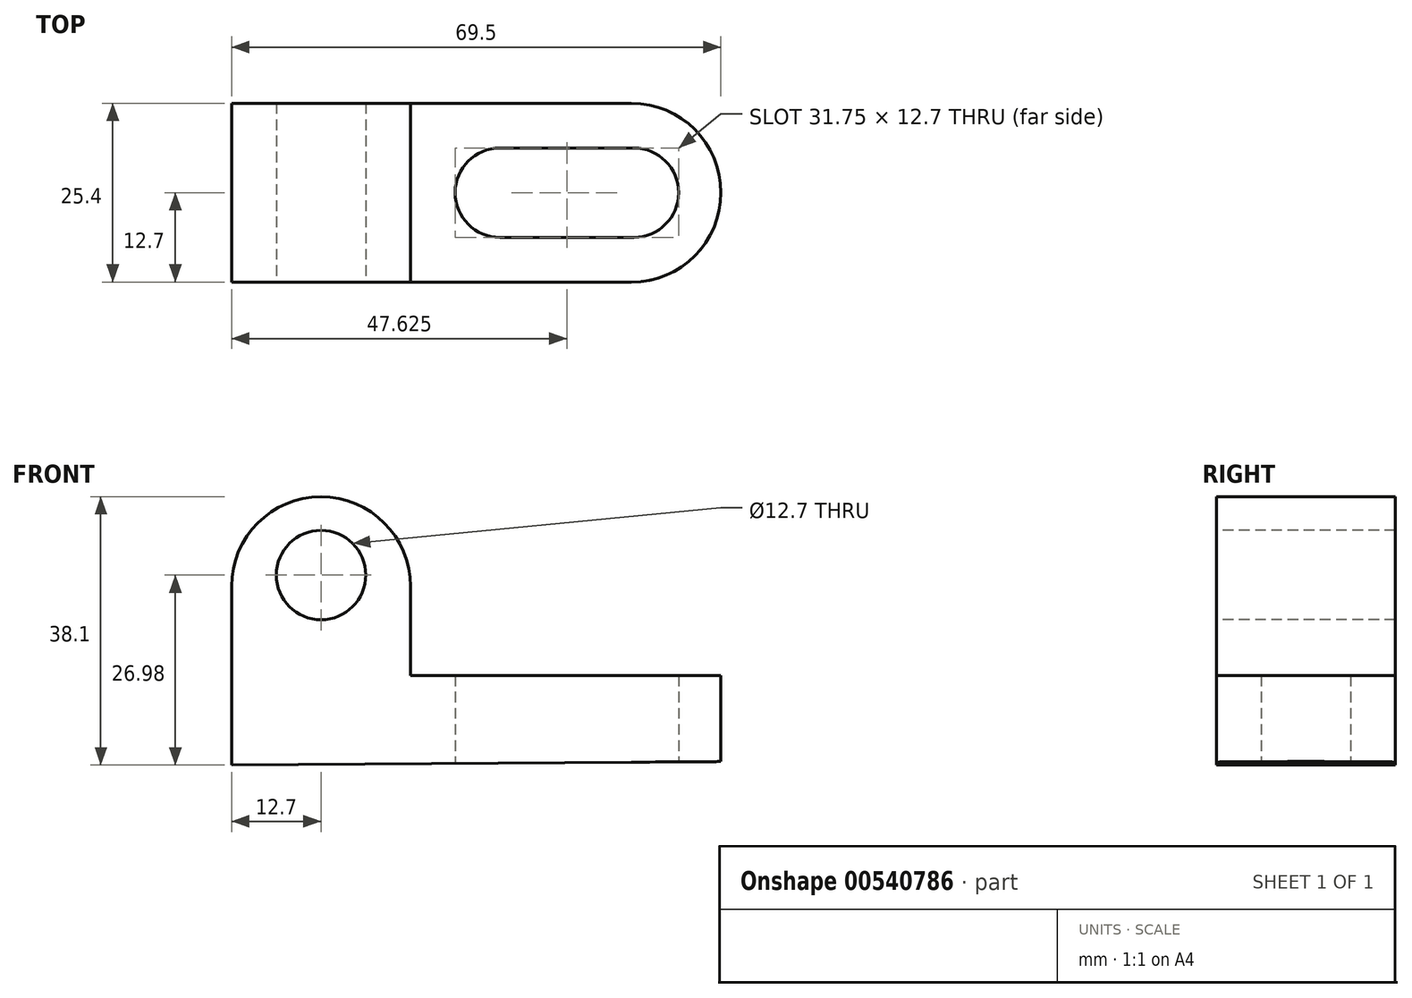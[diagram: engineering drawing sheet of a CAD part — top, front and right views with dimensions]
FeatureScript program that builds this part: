
annotation { "Feature Type Name" : "Feature", "Feature Type Description" : "" }
export const myFeature = defineFeature(function(context is Context, id is Id, definition is map)
    precondition{}
    {
        {
            var Q0;
            Q0=qCreatedBy(makeId("Front.planeOp"),FACE);
            var sketch = newSketch(context, id + "F0", { "sketchPlane" : qUnion([Q0])});
            skLineSegment(sketch, "E0", {"start": v(0, 38.1) * mm, "end": v(0, 0) * mm});
            skLineSegment(sketch, "E1", {"start": v(0, 38.1) * mm, "end": v(25.4, 38.1) * mm});
            skLineSegment(sketch, "E2", {"start": v(25.4, 38.1) * mm, "end": v(25.4, 12.7) * mm});
            skLineSegment(sketch, "E3", {"start": v(25.05, 12.7) * mm, "end": v(69.5, 12.7) * mm});
            skLineSegment(sketch, "E4", {"start": v(69.5, 12.7) * mm, "end": v(69.5, 0) * mm});
            skLineSegment(sketch, "E5", {"start": v(69.85, 0.49) * mm, "end": v(0, 0) * mm});
            skSolve(sketch);
        }
        {
            var Q0;
            {var subQ4=sQuery(id+"F0.wireOp",EDGE,"E0");Q0=makeQuery(id+"F0.imprint","IMPRINT",FACE,{"disambiguationData":[TD([[makeQuery(id+"F0.imprint","IMPRINT",EDGE,{"derivedFrom":subQ4}),1.0]])]});}
            extrude(context, id + "F1", {"entities" : qUnion([Q0]), "depth" : 25.4 * mm, "offsetDistance" : 25.4 * mm});
        }
        {
            var Q0;
            Q0=makeQuery(id+"F1.opExtrude","SWEPT_FACE",FACE,{"disambiguationData":[OSD([sQuery(id+"F0.wireOp",EDGE,"E3")])]});
            var sketch = newSketch(context, id + "F2", { "sketchPlane" : qUnion([Q0])});
            skLineSegment(sketch, "E6", {"start": v(69.5, -25.4) * mm, "end": v(56.8, -25.4) * mm});
            skLineSegment(sketch, "E7", {"start": v(69.5, 0) * mm, "end": v(56.8, 0) * mm});
            skArc(sketch, "E8", {"start": v(56.8, -25.4) * mm, "mid": v(69.5, -12.7) * mm, "end": v(56.8, 0) * mm});
            skSolve(sketch);
        }
        {
            var Q0;
            {var subQ0=sQuery(id+"F2.wireOp",EDGE,"E7");Q0=makeQuery(id+"F2.imprint","IMPRINT",FACE,{"disambiguationData":[TD([[makeQuery(id+"F2.imprint","IMPRINT",EDGE,{"derivedFrom":subQ0}),-1.0]])]});}
            var Q1;
            {var subQ0=sQuery(id+"F2.wireOp",EDGE,"E6");Q1=makeQuery(id+"F2.imprint","IMPRINT",FACE,{"disambiguationData":[TD([[makeQuery(id+"F2.imprint","IMPRINT",EDGE,{"derivedFrom":subQ0}),1.0]])]});}
            extrude(context, id + "F3", {"entities" : qUnion([Q0, Q1]), "operationType" : NewBodyOperationType.REMOVE, "oppositeDirection" : true, "depth" : 25.4 * mm, "offsetDistance" : 25.4 * mm});
        }
        {
            var Q0;
            Q0=makeQuery(id+"F1.opExtrude","CAP_FACE",FACE,{"disambiguationData":[OSD([sQuery(id+"F0.wireOp",EDGE,"E0"),sQuery(id+"F0.wireOp",EDGE,"E1"),sQuery(id+"F0.wireOp",EDGE,"E2"),sQuery(id+"F0.wireOp",EDGE,"E3"),sQuery(id+"F0.wireOp",EDGE,"E4"),sQuery(id+"F0.wireOp",EDGE,"E5")])],"isStart":false});
            var sketch = newSketch(context, id + "F4", { "sketchPlane" : qUnion([Q0])});
            skCircle(sketch, "E9", {"center": v(12.7, 26.98) * mm, "radius": 6.35 * mm});
            skLineSegment(sketch, "E10", {"start": v(12.7, 26.98) * mm, "end": v(19.05, 26.98) * mm});
            skLineSegment(sketch, "E11", {"start": v(6.36, 27.28) * mm, "end": v(0, 27.28) * mm});
            skLineSegment(sketch, "E12", {"start": v(19.05, 26.98) * mm, "end": v(25.4, 26.98) * mm});
            skSolve(sketch);
        }
        {
            var Q0;
            {var subQ0=sQuery(id+"F4.wireOp",EDGE,"E9");var subQ1=makeQuery(id+"F4.imprint","INTERSECT",VERTEX,{"derivedFrom":[subQ0,sQuery(id+"F4.wireOp",EDGE,"E12")]});Q0=makeQuery(id+"F4.imprint","IMPRINT",FACE,{"disambiguationData":[TD([[makeQuery(id+"F4.imprint","IMPRINT",EDGE,{"disambiguationData":[TD([[subQ1,-1.0]])],"derivedFrom":subQ0}),1.0]])]});}
            extrude(context, id + "F5", {"entities" : qUnion([Q0]), "operationType" : NewBodyOperationType.REMOVE, "oppositeDirection" : true, "depth" : 101.6 * mm, "offsetDistance" : 25.4 * mm});
        }
        {
            var Q0;
            Q0=makeQuery(id+"F1.opExtrude","CAP_FACE",FACE,{"disambiguationData":[OSD([sQuery(id+"F0.wireOp",EDGE,"E0"),sQuery(id+"F0.wireOp",EDGE,"E1"),sQuery(id+"F0.wireOp",EDGE,"E2"),sQuery(id+"F0.wireOp",EDGE,"E3"),sQuery(id+"F0.wireOp",EDGE,"E4"),sQuery(id+"F0.wireOp",EDGE,"E5")])],"isStart":false});
            var sketch = newSketch(context, id + "F6", { "sketchPlane" : qUnion([Q0])});
            skArc(sketch, "E13", {"start": v(25.4, 25.4) * mm, "mid": v(12.7, 38.1) * mm, "end": v(0, 25.4) * mm});
            skLineSegment(sketch, "E14", {"start": v(12.7, 25.4) * mm, "end": v(12.7, 38.1) * mm});
            skLineSegment(sketch, "E15", {"start": v(0, 25.4) * mm, "end": v(0, 0) * mm});
            skLineSegment(sketch, "E16", {"start": v(25.4, 25.4) * mm, "end": v(25.4, 0) * mm});
            skSolve(sketch);
        }
        {
            var Q0;
            {var subQ1=makeQuery(id+"F1.opExtrude","CAP_EDGE",EDGE,{"disambiguationData":[OSD([sQuery(id+"F0.wireOp",EDGE,"E2")])],"isStart":false});var subQ3=makeQuery(id+"F1.opExtrude","CAP_EDGE",EDGE,{"disambiguationData":[OSD([sQuery(id+"F0.wireOp",EDGE,"E1")])],"isStart":false});var subQ5=makeQuery(id+"F6.imprint","INTERSECT",VERTEX,{"derivedFrom":[subQ3,subQ1]});Q0=makeQuery(id+"F6.imprint","IMPRINT",FACE,{"disambiguationData":[TD([[makeQuery(id+"F6.imprint","IMPRINT",EDGE,{"disambiguationData":[TD([[subQ5,1.0]])],"derivedFrom":subQ3}),-1.0]])]});}
            var Q1;
            {var subQ1=makeQuery(id+"F1.opExtrude","CAP_EDGE",EDGE,{"disambiguationData":[OSD([sQuery(id+"F0.wireOp",EDGE,"E0")])],"isStart":false});var subQ3=makeQuery(id+"F1.opExtrude","CAP_EDGE",EDGE,{"disambiguationData":[OSD([sQuery(id+"F0.wireOp",EDGE,"E1")])],"isStart":false});var subQ5=makeQuery(id+"F6.imprint","INTERSECT",VERTEX,{"derivedFrom":[subQ1,subQ3]});Q1=makeQuery(id+"F6.imprint","IMPRINT",FACE,{"disambiguationData":[TD([[makeQuery(id+"F6.imprint","IMPRINT",EDGE,{"disambiguationData":[TD([[subQ5,-1.0]])],"derivedFrom":subQ3}),-1.0]])]});}
            extrude(context, id + "F7", {"entities" : qUnion([Q0, Q1]), "operationType" : NewBodyOperationType.REMOVE, "depth" : 127 * mm, "offsetDistance" : 25.4 * mm});
        }
        {
            var Q0;
            {var subQ1=makeQuery(id+"F1.opExtrude","CAP_EDGE",EDGE,{"disambiguationData":[OSD([sQuery(id+"F0.wireOp",EDGE,"E0")])],"isStart":false});var subQ3=makeQuery(id+"F1.opExtrude","CAP_EDGE",EDGE,{"disambiguationData":[OSD([sQuery(id+"F0.wireOp",EDGE,"E1")])],"isStart":false});var subQ5=makeQuery(id+"F6.imprint","INTERSECT",VERTEX,{"derivedFrom":[subQ1,subQ3]});Q0=makeQuery(id+"F6.imprint","IMPRINT",FACE,{"disambiguationData":[TD([[makeQuery(id+"F6.imprint","IMPRINT",EDGE,{"disambiguationData":[TD([[subQ5,-1.0]])],"derivedFrom":subQ3}),-1.0]])]});}
            var Q1;
            {var subQ1=makeQuery(id+"F1.opExtrude","CAP_EDGE",EDGE,{"disambiguationData":[OSD([sQuery(id+"F0.wireOp",EDGE,"E2")])],"isStart":false});var subQ3=makeQuery(id+"F1.opExtrude","CAP_EDGE",EDGE,{"disambiguationData":[OSD([sQuery(id+"F0.wireOp",EDGE,"E1")])],"isStart":false});var subQ5=makeQuery(id+"F6.imprint","INTERSECT",VERTEX,{"derivedFrom":[subQ3,subQ1]});Q1=makeQuery(id+"F6.imprint","IMPRINT",FACE,{"disambiguationData":[TD([[makeQuery(id+"F6.imprint","IMPRINT",EDGE,{"disambiguationData":[TD([[subQ5,1.0]])],"derivedFrom":subQ3}),-1.0]])]});}
            extrude(context, id + "F8", {"entities" : qUnion([Q0, Q1]), "operationType" : NewBodyOperationType.REMOVE, "oppositeDirection" : true, "depth" : 25.4 * mm, "offsetDistance" : 25.4 * mm});
        }
        {
            var Q0;
            Q0=qCreatedBy(makeId("Top.planeOp"),FACE);
            var sketch = newSketch(context, id + "F9", { "sketchPlane" : qUnion([Q0])});
            skCircle(sketch, "E17", {"center": v(38.1, -12.7) * mm, "radius": 6.35 * mm});
            skCircle(sketch, "E18", {"center": v(57.15, -12.7) * mm, "radius": 6.35 * mm});
            skLineSegment(sketch, "E19", {"start": v(57.15, -12.7) * mm, "end": v(57.15, -6.35) * mm});
            skLineSegment(sketch, "E20", {"start": v(57.15, -6.35) * mm, "end": v(38.1, -6.35) * mm});
            skLineSegment(sketch, "E21", {"start": v(38.1, -19.05) * mm, "end": v(57.15, -19.05) * mm});
            skSolve(sketch);
        }
        {
            var Q0;
            {var subQ0=sQuery(id+"F9.wireOp",EDGE,"E18");var subQ1=makeQuery(id+"F9.imprint","INTERSECT",VERTEX,{"derivedFrom":[subQ0,sQuery(id+"F9.wireOp",EDGE,"E20")]});Q0=makeQuery(id+"F9.imprint","IMPRINT",FACE,{"disambiguationData":[TD([[makeQuery(id+"F9.imprint","IMPRINT",EDGE,{"disambiguationData":[TD([[subQ1,-1.0]])],"derivedFrom":subQ0}),1.0]])]});}
            var Q1;
            {var subQ0=sQuery(id+"F9.wireOp",EDGE,"E20");Q1=makeQuery(id+"F9.imprint","IMPRINT",FACE,{"disambiguationData":[TD([[makeQuery(id+"F9.imprint","IMPRINT",EDGE,{"derivedFrom":subQ0}),1.0]])]});}
            var Q2;
            {var subQ0=sQuery(id+"F9.wireOp",EDGE,"E17");var subQ1=makeQuery(id+"F9.imprint","INTERSECT",VERTEX,{"derivedFrom":[subQ0,sQuery(id+"F9.wireOp",EDGE,"E20")]});Q2=makeQuery(id+"F9.imprint","IMPRINT",FACE,{"disambiguationData":[TD([[makeQuery(id+"F9.imprint","IMPRINT",EDGE,{"disambiguationData":[TD([[subQ1,-1.0]])],"derivedFrom":subQ0}),1.0]])]});}
            extrude(context, id + "F10", {"entities" : qUnion([Q0, Q1, Q2]), "operationType" : NewBodyOperationType.REMOVE, "depth" : 25.4 * mm, "offsetDistance" : 25.4 * mm});
        }
    });
